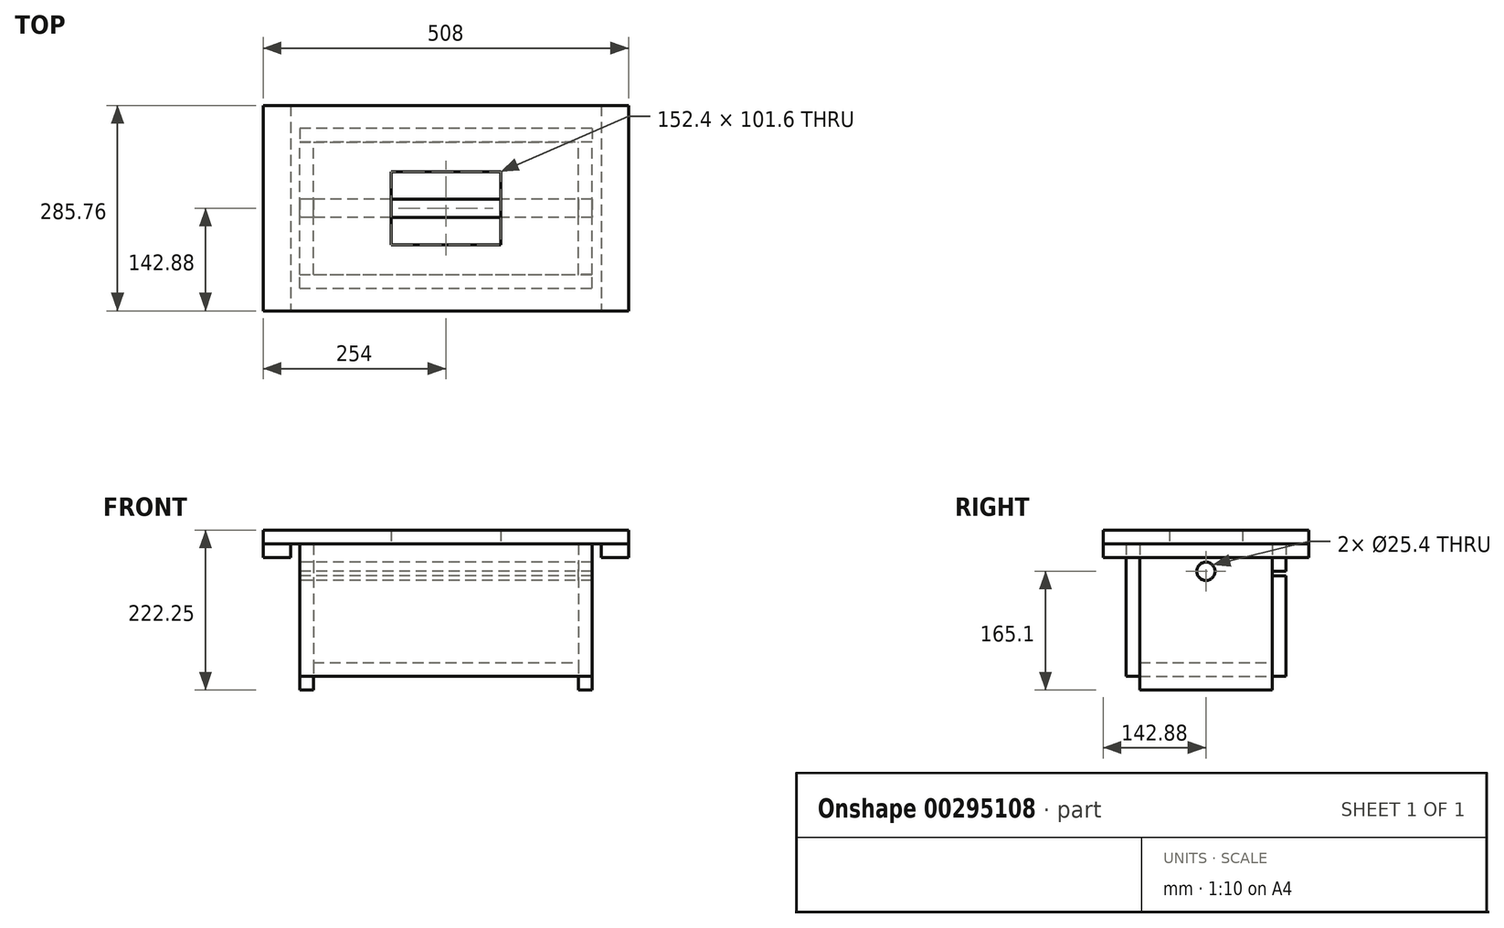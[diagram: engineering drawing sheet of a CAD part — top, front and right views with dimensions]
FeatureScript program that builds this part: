
annotation { "Feature Type Name" : "Feature", "Feature Type Description" : "" }
export const myFeature = defineFeature(function(context is Context, id is Id, definition is map)
    precondition{}
    {
        {
            var Q0;
            Q0=qCreatedBy(makeId("Top.planeOp"),FACE);
            var sketch = newSketch(context, id + "F0", { "sketchPlane" : qUnion([Q0])});
            skLineSegment(sketch, "E0.bottom", {"start": v(-184.15, -92.08) * mm, "end": v(184.15, -92.08) * mm});
            skLineSegment(sketch, "E0.top", {"start": v(-184.15, 92.08) * mm, "end": v(184.15, 92.08) * mm});
            skLineSegment(sketch, "E0.left", {"start": v(-184.15, -92.08) * mm, "end": v(-184.15, 92.08) * mm});
            skLineSegment(sketch, "E0.right", {"start": v(184.15, -92.08) * mm, "end": v(184.15, 92.08) * mm});
            skPoint(sketch, "E0.middle", {"position": v(0, 0) * mm});
            skSolve(sketch);
        }
        {
            var Q0;
            Q0 = qSketchRegion(id + "F0", true);
            extrude(context, id + "F1", {"entities" : qUnion([Q0]), "depth" : 19.05 * mm});
        }
        {
            var Q0;
            Q0=makeQuery(id+"F1.opExtrude","SWEPT_FACE",FACE,{"disambiguationData":[OSD([sQuery(id+"F0.wireOp",EDGE,"E0.right")])]});
            var sketch = newSketch(context, id + "F2", { "sketchPlane" : qUnion([Q0])});
            skLineSegment(sketch, "E1.bottom", {"start": v(-92.08, 184.15) * mm, "end": v(92.07, 184.15) * mm});
            skLineSegment(sketch, "E1.top", {"start": v(-92.08, -19.05) * mm, "end": v(92.07, -19.05) * mm});
            skLineSegment(sketch, "E1.left", {"start": v(-92.08, 184.15) * mm, "end": v(-92.08, -19.05) * mm});
            skLineSegment(sketch, "E1.right", {"start": v(92.07, 184.15) * mm, "end": v(92.07, -19.05) * mm});
            skLineSegment(sketch, "E2", {"start": v(0, 0) * mm, "end": v(0, -19.05) * mm, "construction": true});
            skPoint(sketch, "E2.endSnap0", {"position": v(0, 0) * mm});
            skSolve(sketch);
        }
        {
            var Q0;
            Q0 = qSketchRegion(id + "F2", true);
            extrude(context, id + "F3", {"entities" : qUnion([Q0]), "depth" : 19.05 * mm});
        }
        {
            var Q0;
            Q0=makeQuery(id+"F1.opExtrude","SWEPT_FACE",FACE,{"disambiguationData":[OSD([sQuery(id+"F0.wireOp",EDGE,"E0.left")])]});
            var sketch = newSketch(context, id + "F4", { "sketchPlane" : qUnion([Q0])});
            skLineSegment(sketch, "E3.0", {"start": v(92.08, 184.15) * mm, "end": v(-92.07, 184.15) * mm});
            skLineSegment(sketch, "E3.1", {"start": v(92.08, -19.05) * mm, "end": v(-92.07, -19.05) * mm});
            skLineSegment(sketch, "E3.2", {"start": v(92.08, 184.15) * mm, "end": v(92.08, -19.05) * mm});
            skLineSegment(sketch, "E3.3", {"start": v(-92.07, 184.15) * mm, "end": v(-92.07, -19.05) * mm});
            skLineSegment(sketch, "E3.4", {"start": v(0, 0) * mm, "end": v(0, -19.05) * mm});
            skPoint(sketch, "E3.5", {"position": v(0, 0) * mm});
            skSolve(sketch);
        }
        {
            var Q0;
            Q0 = qSketchRegion(id + "F4", true);
            extrude(context, id + "F5", {"entities" : qUnion([Q0]), "depth" : 19.05 * mm});
        }
        {
            var Q0;
            Q0=makeQuery(id+"F5.opExtrude","CAP_FACE",FACE,{"disambiguationData":[OSD([sQuery(id+"F4.wireOp",EDGE,"E3.0"),sQuery(id+"F4.wireOp",EDGE,"E3.1"),sQuery(id+"F4.wireOp",EDGE,"E3.2"),sQuery(id+"F4.wireOp",EDGE,"E3.3")])],"isStart":false});
            var sketch = newSketch(context, id + "F6", { "sketchPlane" : qUnion([Q0])});
            skCircle(sketch, "E4", {"center": v(0, 146.05) * mm, "radius": 12.7 * mm});
            skSolve(sketch);
        }
        {
            var Q0;
            Q0 = qSketchRegion(id + "F6", true);
            extrude(context, id + "F7", {"entities" : qUnion([Q0]), "operationType" : NewBodyOperationType.REMOVE, "endBound" : BoundingType.THROUGH_ALL, "oppositeDirection" : true, "depth" : 25.4 * mm});
        }
        {
            var Q0;
            Q0=makeQuery(id+"F5.opExtrude","CAP_FACE",FACE,{"disambiguationData":[OSD([sQuery(id+"F4.wireOp",EDGE,"E3.0"),sQuery(id+"F4.wireOp",EDGE,"E3.1"),sQuery(id+"F4.wireOp",EDGE,"E3.2"),sQuery(id+"F4.wireOp",EDGE,"E3.3")])],"isStart":false});
            var sketch = newSketch(context, id + "F8", { "sketchPlane" : qUnion([Q0])});
            skCircle(sketch, "E5.0", {"center": v(0, 146.05) * mm, "radius": 12.7 * mm});
            skSolve(sketch);
        }
        {
            var Q0;
            Q0 = qSketchRegion(id + "F8", true);
            var Q1;
            Q1=makeQuery(id+"F3.opExtrude","CAP_FACE",FACE,{"disambiguationData":[OSD([sQuery(id+"F2.wireOp",EDGE,"E1.bottom"),sQuery(id+"F2.wireOp",EDGE,"E1.top"),sQuery(id+"F2.wireOp",EDGE,"E1.left"),sQuery(id+"F2.wireOp",EDGE,"E1.right")])],"isStart":false});
            extrude(context, id + "F9", {"entities" : qUnion([Q0]), "endBound" : BoundingType.UP_TO_SURFACE, "oppositeDirection" : true, "endBoundEntityFace" : qUnion([Q1]), "depth" : 25.4 * mm});
        }
        {
            var Q0;
            Q0=makeQuery(id+"F1.opExtrude","SWEPT_FACE",FACE,{"disambiguationData":[OSD([sQuery(id+"F0.wireOp",EDGE,"E0.top")])]});
            var sketch = newSketch(context, id + "F10", { "sketchPlane" : qUnion([Q0])});
            skLineSegment(sketch, "E6.bottom", {"start": v(-203.2, 139.7) * mm, "end": v(203.2, 139.7) * mm});
            skLineSegment(sketch, "E6.top", {"start": v(-203.2, 0) * mm, "end": v(203.2, 0) * mm});
            skLineSegment(sketch, "E6.left", {"start": v(-203.2, 139.7) * mm, "end": v(-203.2, 0) * mm});
            skLineSegment(sketch, "E6.right", {"start": v(203.2, 139.7) * mm, "end": v(203.2, 0) * mm});
            skSolve(sketch);
        }
        {
            var Q0;
            Q0 = qSketchRegion(id + "F10", true);
            extrude(context, id + "F11", {"entities" : qUnion([Q0]), "depth" : 19.05 * mm});
        }
        {
            var Q0;
            Q0=makeQuery(id+"F1.opExtrude","SWEPT_FACE",FACE,{"disambiguationData":[OSD([sQuery(id+"F0.wireOp",EDGE,"E0.bottom")])]});
            var sketch = newSketch(context, id + "F12", { "sketchPlane" : qUnion([Q0])});
            skLineSegment(sketch, "E7.2", {"start": v(-203.2, 0) * mm, "end": v(210.42, 0) * mm});
            skLineSegment(sketch, "E8.0", {"start": v(-203.2, 184.15) * mm, "end": v(-203.2, 0) * mm});
            skLineSegment(sketch, "E9.0", {"start": v(203.2, 184.15) * mm, "end": v(203.2, 0) * mm});
            skLineSegment(sketch, "E10", {"start": v(-203.2, 184.15) * mm, "end": v(203.2, 184.15) * mm});
            skPoint(sketch, "E11.orphan", {"position": v(-203.2, -19.05) * mm});
            skPoint(sketch, "E12.orphan", {"position": v(203.2, -19.05) * mm});
            skPoint(sketch, "E13.orphan", {"position": v(184.15, 0) * mm});
            skPoint(sketch, "E14.orphan", {"position": v(-184.15, 0) * mm});
            skSolve(sketch);
        }
        {
            var Q0;
            Q0 = qSketchRegion(id + "F12", true);
            extrude(context, id + "F13", {"entities" : qUnion([Q0]), "depth" : 19.05 * mm});
        }
        {
            var Q0;
            Q0=makeQuery(id+"F3.opExtrude","SWEPT_FACE",FACE,{"disambiguationData":[OSD([sQuery(id+"F2.wireOp",EDGE,"E1.bottom")])]});
            var sketch = newSketch(context, id + "F14", { "sketchPlane" : qUnion([Q0])});
            skLineSegment(sketch, "E15", {"start": v(386.87, 0) * mm, "end": v(0, 0) * mm, "construction": true});
            skLineSegment(sketch, "E16.top", {"start": v(254, -142.87) * mm, "end": v(-254, -142.88) * mm});
            skLineSegment(sketch, "E16.left", {"start": v(254, 142.88) * mm, "end": v(254, -142.88) * mm});
            skLineSegment(sketch, "E16.right", {"start": v(-254, 142.88) * mm, "end": v(-254, -142.88) * mm});
            skLineSegment(sketch, "E17", {"start": v(0, 0) * mm, "end": v(0, -454.57) * mm, "construction": true});
            skLineSegment(sketch, "E18.MirrorCS", {"start": v(254, 142.88) * mm, "end": v(-254, 142.88) * mm});
            skLineSegment(sketch, "E19.bottom", {"start": v(-76.2, 50.8) * mm, "end": v(76.2, 50.8) * mm});
            skLineSegment(sketch, "E19.top", {"start": v(-76.2, -50.8) * mm, "end": v(76.2, -50.8) * mm});
            skLineSegment(sketch, "E19.left", {"start": v(-76.2, 50.8) * mm, "end": v(-76.2, -50.8) * mm});
            skLineSegment(sketch, "E19.right", {"start": v(76.2, 50.8) * mm, "end": v(76.2, -50.8) * mm});
            skPoint(sketch, "E19.middle", {"position": v(0, 0) * mm});
            skSolve(sketch);
        }
        {
            var Q0;
            Q0 = qSketchRegion(id + "F14", true);
            extrude(context, id + "F15", {"entities" : qUnion([Q0]), "depth" : 19.05 * mm});
        }
        {
            var Q0;
            Q0=makeQuery(id+"F15.opExtrude","CAP_FACE",FACE,{"disambiguationData":[OSD([sQuery(id+"F14.wireOp",EDGE,"E16.top"),sQuery(id+"F14.wireOp",EDGE,"E16.left"),sQuery(id+"F14.wireOp",EDGE,"E16.right"),sQuery(id+"F14.wireOp",EDGE,"E18.MirrorCS"),sQuery(id+"F14.wireOp",EDGE,"E19.bottom"),sQuery(id+"F14.wireOp",EDGE,"E19.top"),sQuery(id+"F14.wireOp",EDGE,"E19.left"),sQuery(id+"F14.wireOp",EDGE,"E19.right")])],"isStart":true});
            var sketch = newSketch(context, id + "F16", { "sketchPlane" : qUnion([Q0])});
            skLineSegment(sketch, "E20.0", {"start": v(-254, -142.88) * mm, "end": v(-254, 142.88) * mm});
            skLineSegment(sketch, "E20.1", {"start": v(-215.9, -142.88) * mm, "end": v(-254, -142.88) * mm});
            skLineSegment(sketch, "E20.2", {"start": v(-215.9, 142.88) * mm, "end": v(-254, 142.88) * mm});
            skLineSegment(sketch, "E21", {"start": v(-215.9, -142.87) * mm, "end": v(-215.9, 142.87) * mm});
            skPoint(sketch, "E22.orphan", {"position": v(254, -142.88) * mm});
            skPoint(sketch, "E23.orphan", {"position": v(254, 142.87) * mm});
            skLineSegment(sketch, "E24", {"start": v(0, -269.93) * mm, "end": v(0, 0) * mm, "construction": true});
            skLineSegment(sketch, "E25.MirrorCS", {"start": v(215.9, 142.87) * mm, "end": v(254, 142.87) * mm});
            skLineSegment(sketch, "E26.MirrorCS", {"start": v(215.9, -142.87) * mm, "end": v(254, -142.87) * mm});
            skPoint(sketch, "E27.MirrorP", {"position": v(-254, 142.87) * mm});
            skPoint(sketch, "E28.MirrorP", {"position": v(-254, -142.88) * mm});
            skLineSegment(sketch, "E29.MirrorCS", {"start": v(254, -142.88) * mm, "end": v(254, 142.88) * mm});
            skLineSegment(sketch, "E30.MirrorCS", {"start": v(215.9, -142.87) * mm, "end": v(215.9, 142.87) * mm});
            skSolve(sketch);
        }
        {
            var Q0;
            Q0 = qSketchRegion(id + "F16", true);
            extrude(context, id + "F17", {"entities" : qUnion([Q0]), "depth" : 19.05 * mm});
        }
        {
            var Q0;
            Q0=makeQuery(id+"F3.opExtrude","SWEPT_FACE",FACE,{"disambiguationData":[OSD([sQuery(id+"F2.wireOp",EDGE,"E1.right")])]});
            var sketch = newSketch(context, id + "F18", { "sketchPlane" : qUnion([Q0])});
            skLineSegment(sketch, "E31.bottom", {"start": v(-203.2, 184.15) * mm, "end": v(203.2, 184.15) * mm});
            skLineSegment(sketch, "E31.top", {"start": v(-203.2, 146.05) * mm, "end": v(203.2, 146.05) * mm});
            skLineSegment(sketch, "E31.left", {"start": v(-203.2, 184.15) * mm, "end": v(-203.2, 146.05) * mm});
            skLineSegment(sketch, "E31.right", {"start": v(203.2, 184.15) * mm, "end": v(203.2, 146.05) * mm});
            skLineSegment(sketch, "E32", {"start": v(0, 289.44) * mm, "end": v(0, 0) * mm, "construction": true});
            skSolve(sketch);
        }
        {
            var Q0;
            Q0 = qSketchRegion(id + "F18", true);
            extrude(context, id + "F19", {"entities" : qUnion([Q0]), "depth" : 19.05 * mm});
        }
    });
